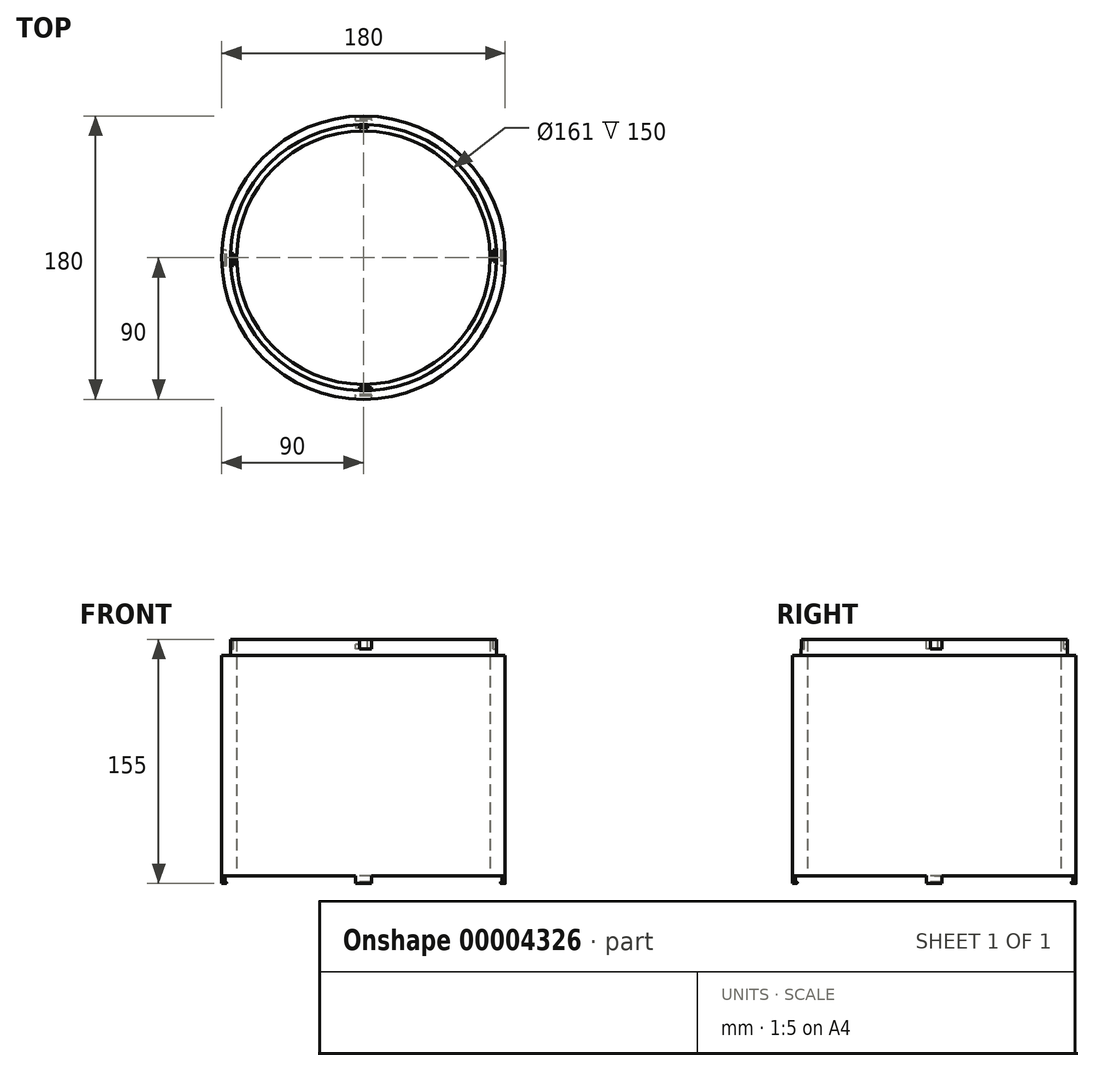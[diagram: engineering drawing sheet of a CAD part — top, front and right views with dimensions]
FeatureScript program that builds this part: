
annotation { "Feature Type Name" : "Feature", "Feature Type Description" : "" }
export const myFeature = defineFeature(function(context is Context, id is Id, definition is map)
    precondition{}
    {
        {
            var Q0;
            Q0=qCreatedBy(makeId("Top.planeOp"),FACE);
            var sketch = newSketch(context, id + "F0", { "sketchPlane" : qUnion([Q0])});
            skCircle(sketch, "E0", {"center": v(0, 0) * mm, "radius": 90 * mm});
            skSolve(sketch);
        }
        {
            var Q0;
            Q0=makeQuery(id+"F0.imprint","IMPRINT",FACE,{"disambiguationData":[TD([[makeQuery(id+"F0.imprint","IMPRINT",EDGE,{"derivedFrom":sQuery(id+"F0.wireOp",EDGE,"E0")}),1.0]])]});
            extrude(context, id + "F1", {"entities" : qUnion([Q0]), "oppositeDirection" : true, "depth" : 150 * mm});
        }
        {
            var Q0;
            Q0=makeQuery(id+"F1.opExtrude","CAP_FACE",FACE,{"disambiguationData":[OSD([sQuery(id+"F0.wireOp",EDGE,"E0")])],"isStart":true});
            var sketch = newSketch(context, id + "F2", { "sketchPlane" : qUnion([Q0])});
            skCircle(sketch, "E1.0", {"center": v(0, 0) * mm, "radius": 80 * mm});
            skSolve(sketch);
        }
        {
            var Q0;
            Q0=makeQuery(id+"F2.imprint","IMPRINT",FACE,{"disambiguationData":[TD([[makeQuery(id+"F2.imprint","IMPRINT",EDGE,{"derivedFrom":sQuery(id+"F2.wireOp",EDGE,"E1.0")}),1.0]])]});
            extrude(context, id + "F3", {"entities" : qUnion([Q0]), "operationType" : NewBodyOperationType.REMOVE, "oppositeDirection" : true, "depth" : 100 * mm});
        }
        {
            var Q0;
            Q0=makeQuery(id+"F1.opExtrude","CAP_FACE",FACE,{"disambiguationData":[OSD([sQuery(id+"F0.wireOp",EDGE,"E0")])],"isStart":true});
            var sketch = newSketch(context, id + "F4", { "sketchPlane" : qUnion([Q0])});
            skCircle(sketch, "E2.0", {"center": v(0, 0) * mm, "radius": 84.5 * mm});
            skSolve(sketch);
        }
        {
            var Q0;
            Q0=makeQuery(id+"F4.imprint","IMPRINT",FACE,{"disambiguationData":[TD([[makeQuery(id+"F4.imprint","IMPRINT",EDGE,{"derivedFrom":sQuery(id+"F4.wireOp",EDGE,"E2.0")}),-1.0]])]});
            extrude(context, id + "F5", {"entities" : qUnion([Q0]), "operationType" : NewBodyOperationType.REMOVE, "oppositeDirection" : true, "depth" : 10 * mm});
        }
        {
            var Q0;
            Q0=makeQuery(id+"F1.opExtrude","CAP_FACE",FACE,{"disambiguationData":[OSD([sQuery(id+"F0.wireOp",EDGE,"E0")])],"isStart":false});
            var sketch = newSketch(context, id + "F6", { "sketchPlane" : qUnion([Q0])});
            skCircle(sketch, "E3.0", {"center": v(0, 0) * mm, "radius": 80.5 * mm});
            skSolve(sketch);
        }
        {
            var Q0;
            Q0=makeQuery(id+"F6.imprint","IMPRINT",FACE,{"disambiguationData":[TD([[makeQuery(id+"F6.imprint","IMPRINT",EDGE,{"derivedFrom":sQuery(id+"F6.wireOp",EDGE,"E3.0")}),1.0]])]});
            extrude(context, id + "F7", {"entities" : qUnion([Q0]), "operationType" : NewBodyOperationType.REMOVE, "oppositeDirection" : true, "depth" : 179.6 * mm});
        }
        {
            var Q0;
            Q0=makeQuery(id+"F1.opExtrude","CAP_FACE",FACE,{"disambiguationData":[OSD([sQuery(id+"F0.wireOp",EDGE,"E0")])],"isStart":false});
            var sketch = newSketch(context, id + "F8", { "sketchPlane" : qUnion([Q0])});
            skCircle(sketch, "E4.0", {"center": v(0, 0) * mm, "radius": 85 * mm});
            skLineSegment(sketch, "E5.0", {"start": v(-88, 0) * mm, "end": v(-88, -5) * mm});
            skLineSegment(sketch, "E5.1", {"start": v(-88, 0) * mm, "end": v(-88, 5) * mm});
            skLineSegment(sketch, "E6.0", {"start": v(-90, 0) * mm, "end": v(-90, 5) * mm});
            skLineSegment(sketch, "E6.1", {"start": v(-90, 0) * mm, "end": v(-90, -5) * mm});
            skLineSegment(sketch, "E7", {"start": v(-90, 5) * mm, "end": v(-88, 5) * mm});
            skLineSegment(sketch, "E8", {"start": v(-88, -5) * mm, "end": v(-90, -5) * mm});
            skLineSegment(sketch, "E9.0", {"start": v(0, 88) * mm, "end": v(-5, 88) * mm});
            skLineSegment(sketch, "E10.0", {"start": v(0, 88) * mm, "end": v(5, 88) * mm});
            skLineSegment(sketch, "E11.0", {"start": v(0, 90) * mm, "end": v(-5, 90) * mm});
            skLineSegment(sketch, "E12.0", {"start": v(0, 90) * mm, "end": v(5, 90) * mm});
            skLineSegment(sketch, "E13", {"start": v(-5, 90) * mm, "end": v(-5, 88) * mm});
            skLineSegment(sketch, "E14", {"start": v(5, 90) * mm, "end": v(5, 88) * mm});
            skLineSegment(sketch, "E15.0", {"start": v(88, 0) * mm, "end": v(88, 5) * mm});
            skLineSegment(sketch, "E16.0", {"start": v(88, 0) * mm, "end": v(88, -5) * mm});
            skLineSegment(sketch, "E17.0", {"start": v(90, 0) * mm, "end": v(90, 5) * mm});
            skLineSegment(sketch, "E18.0", {"start": v(90, 0) * mm, "end": v(90, -5) * mm});
            skLineSegment(sketch, "E19", {"start": v(88, 5) * mm, "end": v(90, 5) * mm});
            skLineSegment(sketch, "E20", {"start": v(88, -5) * mm, "end": v(90, -5) * mm});
            skLineSegment(sketch, "E21.0", {"start": v(0, -88) * mm, "end": v(-5, -88) * mm});
            skLineSegment(sketch, "E21.1", {"start": v(0, -88) * mm, "end": v(5, -88) * mm});
            skLineSegment(sketch, "E22.0", {"start": v(0, -90) * mm, "end": v(-5, -90) * mm});
            skLineSegment(sketch, "E22.1", {"start": v(0, -90) * mm, "end": v(5, -90) * mm});
            skLineSegment(sketch, "E23", {"start": v(-5, -88) * mm, "end": v(-5, -90) * mm});
            skLineSegment(sketch, "E24", {"start": v(5, -88) * mm, "end": v(5, -90) * mm});
            skSolve(sketch);
        }
        {
            var Q0;
            {var subQ6=sQuery(id+"F8.wireOp",EDGE,"E5.0");Q0=makeQuery(id+"F8.imprint","IMPRINT",FACE,{"disambiguationData":[TD([[makeQuery(id+"F8.imprint","IMPRINT",EDGE,{"derivedFrom":subQ6}),-1.0]])]});}
            var Q1;
            {var subQ7=sQuery(id+"F8.wireOp",EDGE,"E21.0");Q1=makeQuery(id+"F8.imprint","IMPRINT",FACE,{"disambiguationData":[TD([[makeQuery(id+"F8.imprint","IMPRINT",EDGE,{"derivedFrom":subQ7}),1.0]])]});}
            var Q2;
            {var subQ7=sQuery(id+"F8.wireOp",EDGE,"E15.0");Q2=makeQuery(id+"F8.imprint","IMPRINT",FACE,{"disambiguationData":[TD([[makeQuery(id+"F8.imprint","IMPRINT",EDGE,{"derivedFrom":subQ7}),-1.0]])]});}
            var Q3;
            {var subQ7=sQuery(id+"F8.wireOp",EDGE,"E9.0");Q3=makeQuery(id+"F8.imprint","IMPRINT",FACE,{"disambiguationData":[TD([[makeQuery(id+"F8.imprint","IMPRINT",EDGE,{"derivedFrom":subQ7}),-1.0]])]});}
            extrude(context, id + "F9", {"entities" : qUnion([Q0, Q1, Q2, Q3]), "operationType" : NewBodyOperationType.ADD, "depth" : 5 * mm});
        }
        {
            var Q0;
            Q0=makeQuery(id+"F9.opExtrude","SWEPT_FACE",FACE,{"disambiguationData":[OSD([sQuery(id+"F8.wireOp",EDGE,"E5.0"),sQuery(id+"F8.wireOp",EDGE,"E5.1")])]});
            var sketch = newSketch(context, id + "F10", { "sketchPlane" : qUnion([Q0])});
            skLineSegment(sketch, "E25.0", {"start": v(-5, -154) * mm, "end": v(5, -154) * mm});
            skSolve(sketch);
        }
        {
            var Q0;
            Q0=makeQuery(id+"F9.opExtrude","SWEPT_FACE",FACE,{"disambiguationData":[OSD([sQuery(id+"F8.wireOp",EDGE,"E21.0"),sQuery(id+"F8.wireOp",EDGE,"E21.1")])]});
            var sketch = newSketch(context, id + "F11", { "sketchPlane" : qUnion([Q0])});
            skLineSegment(sketch, "E26.0", {"start": v(-5, -154) * mm, "end": v(5, -154) * mm});
            skSolve(sketch);
        }
        {
            var Q0;
            Q0=makeQuery(id+"F9.opExtrude","SWEPT_FACE",FACE,{"disambiguationData":[OSD([sQuery(id+"F8.wireOp",EDGE,"E15.0"),sQuery(id+"F8.wireOp",EDGE,"E16.0")])]});
            var sketch = newSketch(context, id + "F12", { "sketchPlane" : qUnion([Q0])});
            skLineSegment(sketch, "E27.0", {"start": v(-5, -154) * mm, "end": v(5, -154) * mm});
            skSolve(sketch);
        }
        {
            var Q0;
            Q0=makeQuery(id+"F9.opExtrude","SWEPT_FACE",FACE,{"disambiguationData":[OSD([sQuery(id+"F8.wireOp",EDGE,"E9.0"),sQuery(id+"F8.wireOp",EDGE,"E10.0")])]});
            var sketch = newSketch(context, id + "F13", { "sketchPlane" : qUnion([Q0])});
            skLineSegment(sketch, "E28.0", {"start": v(-5, -154) * mm, "end": v(5, -154) * mm});
            skSolve(sketch);
        }
        {
            var Q0;
            {var subQ2=sQuery(id+"F13.wireOp",EDGE,"E28.0");Q0=makeQuery(id+"F13.imprint","IMPRINT",FACE,{"disambiguationData":[TD([[makeQuery(id+"F13.imprint","IMPRINT",EDGE,{"derivedFrom":subQ2}),-1.0]])]});}
            extrude(context, id + "F14", {"entities" : qUnion([Q0]), "operationType" : NewBodyOperationType.ADD, "depth" : 1 * mm});
        }
        {
            var Q0;
            {var subQ2=sQuery(id+"F10.wireOp",EDGE,"E25.0");Q0=makeQuery(id+"F10.imprint","IMPRINT",FACE,{"disambiguationData":[TD([[makeQuery(id+"F10.imprint","IMPRINT",EDGE,{"derivedFrom":subQ2}),-1.0]])]});}
            extrude(context, id + "F15", {"entities" : qUnion([Q0]), "operationType" : NewBodyOperationType.ADD, "depth" : 1 * mm});
        }
        {
            var Q0;
            {var subQ2=sQuery(id+"F11.wireOp",EDGE,"E26.0");Q0=makeQuery(id+"F11.imprint","IMPRINT",FACE,{"disambiguationData":[TD([[makeQuery(id+"F11.imprint","IMPRINT",EDGE,{"derivedFrom":subQ2}),-1.0]])]});}
            extrude(context, id + "F16", {"entities" : qUnion([Q0]), "operationType" : NewBodyOperationType.ADD, "depth" : 1 * mm});
        }
        {
            var Q0;
            {var subQ2=sQuery(id+"F12.wireOp",EDGE,"E27.0");Q0=makeQuery(id+"F12.imprint","IMPRINT",FACE,{"disambiguationData":[TD([[makeQuery(id+"F12.imprint","IMPRINT",EDGE,{"derivedFrom":subQ2}),-1.0]])]});}
            extrude(context, id + "F17", {"entities" : qUnion([Q0]), "operationType" : NewBodyOperationType.ADD, "depth" : 1 * mm});
        }
        {
            var Q0;
            Q0=makeQuery(id+"F17.opExtrude","CAP_EDGE",EDGE,{"disambiguationData":[OSD([sQuery(id+"F8.wireOp",EDGE,"E15.0"),sQuery(id+"F8.wireOp",EDGE,"E16.0")])],"isStart":false});
            var Q1;
            Q1=makeQuery(id+"F17.opExtrude","CAP_EDGE",EDGE,{"disambiguationData":[OSD([sQuery(id+"F12.wireOp",EDGE,"E27.0")])],"isStart":false});
            fillet(context, id + "F18", {"entities" : qUnion([Q0, Q1]), "radius" : 0.5 * mm, "tangentPropagation" : true, "allowEdgeOverflow" : false});
        }
        {
            var Q0;
            Q0=makeQuery(id+"F14.opExtrude","CAP_EDGE",EDGE,{"disambiguationData":[OSD([sQuery(id+"F13.wireOp",EDGE,"E28.0")])],"isStart":false});
            var Q1;
            Q1=makeQuery(id+"F14.opExtrude","CAP_EDGE",EDGE,{"disambiguationData":[OSD([sQuery(id+"F8.wireOp",EDGE,"E9.0"),sQuery(id+"F8.wireOp",EDGE,"E10.0")])],"isStart":false});
            fillet(context, id + "F19", {"entities" : qUnion([Q0, Q1]), "radius" : 0.5 * mm, "tangentPropagation" : true, "allowEdgeOverflow" : false});
        }
        {
            var Q0;
            Q0=makeQuery(id+"F15.opExtrude","CAP_EDGE",EDGE,{"disambiguationData":[OSD([sQuery(id+"F10.wireOp",EDGE,"E25.0")])],"isStart":false});
            var Q1;
            Q1=makeQuery(id+"F15.opExtrude","CAP_EDGE",EDGE,{"disambiguationData":[OSD([sQuery(id+"F8.wireOp",EDGE,"E5.0"),sQuery(id+"F8.wireOp",EDGE,"E5.1")])],"isStart":false});
            fillet(context, id + "F20", {"entities" : qUnion([Q0, Q1]), "radius" : 0.5 * mm, "tangentPropagation" : true, "allowEdgeOverflow" : false});
        }
        {
            var Q0;
            Q0=makeQuery(id+"F16.opExtrude","CAP_EDGE",EDGE,{"disambiguationData":[OSD([sQuery(id+"F11.wireOp",EDGE,"E26.0")])],"isStart":false});
            var Q1;
            Q1=makeQuery(id+"F16.opExtrude","CAP_EDGE",EDGE,{"disambiguationData":[OSD([sQuery(id+"F8.wireOp",EDGE,"E21.0"),sQuery(id+"F8.wireOp",EDGE,"E21.1")])],"isStart":false});
            fillet(context, id + "F21", {"entities" : qUnion([Q0, Q1]), "radius" : 0.5 * mm, "tangentPropagation" : true, "allowEdgeOverflow" : false});
        }
        {
            var Q0;
            Q0=makeQuery(id+"F4.imprint","IMPRINT",FACE,{"disambiguationData":[TD([[makeQuery(id+"F4.imprint","IMPRINT",EDGE,{"derivedFrom":sQuery(id+"F4.wireOp",EDGE,"E2.0")}),1.0]])]});
            var sketch = newSketch(context, id + "F22", { "sketchPlane" : qUnion([Q0])});
            skCircle(sketch, "E29.0", {"center": v(0, 0) * mm, "radius": 84.5 * mm});
            skCircle(sketch, "E30.0", {"center": v(0, 0) * mm, "radius": 80 * mm});
            skLineSegment(sketch, "E31", {"start": v(-84.5, 2.5) * mm, "end": v(-81.5, 2.5) * mm});
            skLineSegment(sketch, "E32", {"start": v(-84.5, -2.5) * mm, "end": v(-84.46, -2.5) * mm});
            skLineSegment(sketch, "E33", {"start": v(2.5, 81.81) * mm, "end": v(2.5, 84.5) * mm});
            skLineSegment(sketch, "E34", {"start": v(81.3, -2.5) * mm, "end": v(84.5, -2.5) * mm});
            skLineSegment(sketch, "E35", {"start": v(-2.5, -84.5) * mm, "end": v(-2.5, -82.5) * mm});
            skLineSegment(sketch, "E36", {"start": v(-2.5, -84.5) * mm, "end": v(-2.5, -81.7) * mm});
            skLineSegment(sketch, "E37.0", {"start": v(5, -81.52) * mm, "end": v(5, -84.5) * mm});
            skLineSegment(sketch, "E38.0", {"start": v(81.4, 5) * mm, "end": v(84.5, 5) * mm});
            skLineSegment(sketch, "E39.0", {"start": v(-5, 84.5) * mm, "end": v(-5, 81.47) * mm});
            skLineSegment(sketch, "E40.0", {"start": v(-84.5, -5) * mm, "end": v(-80.8, -5) * mm});
            skCircle(sketch, "E41.0", {"center": v(0, 0) * mm, "radius": 82.5 * mm});
            skSolve(sketch);
        }
        {
            var Q0;
            {var subQ5=sQuery(id+"F22.wireOp",EDGE,"E29.0");var subQ7=makeQuery(id+"F22.imprint","IMPRINT",VERTEX,{"derivedFrom":subQ5});Q0=makeQuery(id+"F22.imprint","IMPRINT",FACE,{"disambiguationData":[TD([[makeQuery(id+"F22.imprint","IMPRINT",EDGE,{"disambiguationData":[TD([[subQ7,1.0]])],"derivedFrom":subQ5}),1.0]])]});}
            var Q1;
            {var subQ3=sQuery(id+"F22.wireOp",EDGE,"E36");var subQ8=makeQuery(id+"F22.imprint","IMPRINT",VERTEX,{"derivedFrom":subQ3});Q1=makeQuery(id+"F22.imprint","IMPRINT",FACE,{"disambiguationData":[TD([[makeQuery(id+"F22.imprint","IMPRINT",EDGE,{"disambiguationData":[TD([[subQ8,1.0]])],"derivedFrom":subQ3}),-1.0]])]});}
            var Q2;
            {var subQ3=sQuery(id+"F22.wireOp",EDGE,"E34");var subQ5=sQuery(id+"F22.wireOp",EDGE,"E29.0");var subQ7=makeQuery(id+"F22.imprint","INTERSECT",VERTEX,{"derivedFrom":[subQ3,subQ5]});Q2=makeQuery(id+"F22.imprint","IMPRINT",FACE,{"disambiguationData":[TD([[makeQuery(id+"F22.imprint","IMPRINT",EDGE,{"disambiguationData":[TD([[subQ7,1.0]])],"derivedFrom":subQ3}),1.0]])]});}
            var Q3;
            {var subQ0=sQuery(id+"F22.wireOp",EDGE,"E29.0");var subQ3=sQuery(id+"F22.wireOp",EDGE,"E33");var subQ4=makeQuery(id+"F22.imprint","INTERSECT",VERTEX,{"derivedFrom":[subQ3,subQ0]});Q3=makeQuery(id+"F22.imprint","IMPRINT",FACE,{"disambiguationData":[TD([[makeQuery(id+"F22.imprint","IMPRINT",EDGE,{"disambiguationData":[TD([[subQ4,1.0]])],"derivedFrom":subQ3}),1.0]])]});}
            extrude(context, id + "F23", {"entities" : qUnion([Q0, Q1, Q2, Q3]), "operationType" : NewBodyOperationType.REMOVE, "oppositeDirection" : true, "depth" : 6 * mm});
        }
        {
            var Q0;
            Q0=makeQuery(id+"F1.opExtrude","CAP_FACE",FACE,{"disambiguationData":[OSD([sQuery(id+"F0.wireOp",EDGE,"E0")])],"isStart":true});
            var sketch = newSketch(context, id + "F24", { "sketchPlane" : qUnion([Q0])});
            skLineSegment(sketch, "E42", {"start": v(5, -84.35) * mm, "end": v(5, -84.35) * mm});
            skLineSegment(sketch, "E43.0", {"start": v(2.5, -84.35) * mm, "end": v(2.5, -84.35) * mm});
            skLineSegment(sketch, "E44.0", {"start": v(84.35, 2.5) * mm, "end": v(84.35, 2.5) * mm});
            skLineSegment(sketch, "E45", {"start": v(84.35, 5) * mm, "end": v(84.35, 5) * mm});
            skLineSegment(sketch, "E46.0", {"start": v(-2.5, 84.35) * mm, "end": v(-2.5, 84.35) * mm});
            skLineSegment(sketch, "E47", {"start": v(-5, 84.35) * mm, "end": v(-5, 84.35) * mm});
            skLineSegment(sketch, "E48.0", {"start": v(-84.35, -2.5) * mm, "end": v(-84.35, -2.5) * mm});
            skLineSegment(sketch, "E49", {"start": v(-84.35, -5) * mm, "end": v(-84.35, -5) * mm});
            skArc(sketch, "E50.0", {"start": v(2.56, 84.46) * mm, "mid": v(-1.28, 84.5) * mm, "end": v(-5.12, 84.34) * mm});
            skLineSegment(sketch, "E51.0", {"start": v(-2.5, 85.02) * mm, "end": v(-2.5, 82.35) * mm});
            skArc(sketch, "E52.0", {"start": v(2.5, 82.46) * mm, "mid": v(-1.25, 82.5) * mm, "end": v(-5, 82.35) * mm});
            skLineSegment(sketch, "E53", {"start": v(-5, 82.35) * mm, "end": v(-5, 84.35) * mm});
            skArc(sketch, "E54.0", {"start": v(-84.46, 2.56) * mm, "mid": v(-84.5, -1.28) * mm, "end": v(-84.34, -5.12) * mm});
            skLineSegment(sketch, "E55.0", {"start": v(-88.37, -2.5) * mm, "end": v(-82.35, -2.5) * mm});
            skArc(sketch, "E56.0", {"start": v(-82.46, 2.5) * mm, "mid": v(-82.5, -1.25) * mm, "end": v(-82.35, -5) * mm});
            skArc(sketch, "E57.0", {"start": v(-2.56, -84.46) * mm, "mid": v(1.28, -84.5) * mm, "end": v(5.12, -84.34) * mm});
            skArc(sketch, "E58.0", {"start": v(-2.5, -82.46) * mm, "mid": v(1.25, -82.5) * mm, "end": v(5, -82.35) * mm});
            skLineSegment(sketch, "E59.0", {"start": v(2.5, -82.35) * mm, "end": v(2.5, -87.42) * mm});
            skArc(sketch, "E60.0", {"start": v(84.46, -2.56) * mm, "mid": v(84.5, 1.28) * mm, "end": v(84.34, 5.12) * mm});
            skArc(sketch, "E61.0", {"start": v(82.46, -2.5) * mm, "mid": v(82.5, 1.25) * mm, "end": v(82.35, 5) * mm});
            skLineSegment(sketch, "E62.0", {"start": v(82.35, 2.5) * mm, "end": v(85.22, 2.5) * mm});
            skSolve(sketch);
        }
        {
            var Q0;
            {var subQ0=makeQuery(id+"F23.boolean.opBoolean","COPY",EDGE,{"derivedFrom":makeQuery(id+"F23.opExtrude","CAP_EDGE",EDGE,{"disambiguationData":[OSD([sQuery(id+"F22.wireOp",EDGE,"E37.0")])],"isStart":true})});Q0=makeQuery(id+"F24.imprint","IMPRINT",FACE,{"disambiguationData":[TD([[makeQuery(id+"F24.imprint","IMPRINT",EDGE,{"derivedFrom":subQ0}),-1.0]])]});}
            var Q1;
            {var subQ0=makeQuery(id+"F23.boolean.opBoolean","COPY",EDGE,{"derivedFrom":makeQuery(id+"F23.opExtrude","CAP_EDGE",EDGE,{"disambiguationData":[OSD([sQuery(id+"F22.wireOp",EDGE,"E38.0")])],"isStart":true})});Q1=makeQuery(id+"F24.imprint","IMPRINT",FACE,{"disambiguationData":[TD([[makeQuery(id+"F24.imprint","IMPRINT",EDGE,{"derivedFrom":subQ0}),-1.0]])]});}
            var Q2;
            {var subQ0=sQuery(id+"F24.wireOp",EDGE,"E53");Q2=makeQuery(id+"F24.imprint","IMPRINT",FACE,{"disambiguationData":[TD([[makeQuery(id+"F24.imprint","IMPRINT",EDGE,{"derivedFrom":subQ0}),1.0]])]});}
            var Q3;
            {var subQ0=makeQuery(id+"F23.boolean.opBoolean","COPY",EDGE,{"derivedFrom":makeQuery(id+"F23.opExtrude","CAP_EDGE",EDGE,{"disambiguationData":[OSD([sQuery(id+"F22.wireOp",EDGE,"E40.0")])],"isStart":true})});Q3=makeQuery(id+"F24.imprint","IMPRINT",FACE,{"disambiguationData":[TD([[makeQuery(id+"F24.imprint","IMPRINT",EDGE,{"derivedFrom":subQ0}),1.0]])]});}
            extrude(context, id + "F25", {"entities" : qUnion([Q0, Q1, Q2, Q3]), "operationType" : NewBodyOperationType.ADD, "oppositeDirection" : true, "depth" : 3 * mm});
        }
    });
